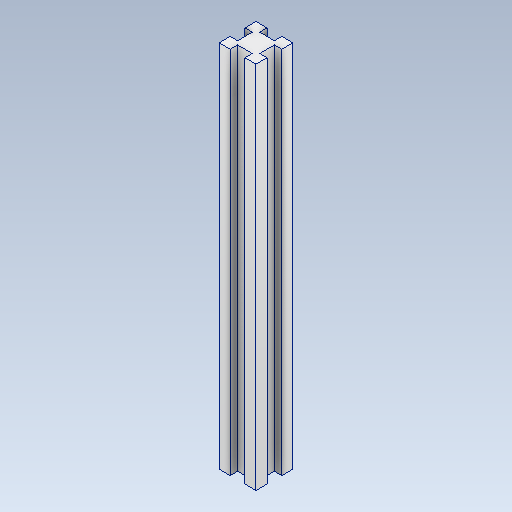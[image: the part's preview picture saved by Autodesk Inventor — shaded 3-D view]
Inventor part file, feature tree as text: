
AUTODESK INVENTOR PART (.ipt)
format: ipt  version: 2021 (Build 250183000, 183)  size: 115,712 bytes
history: native  units: mm
features: other x1, extrude x1, sketch x1
ambient origin geometry x8: Origin, YZ Plane, XZ Plane, XY Plane, X Axis, Y Axis, Z Axis, Center Point
bodies: Body1 (feature_tree)
feature tree (3):
  other  "Bryła1"
  extrude  "Wyciągnięcie proste1"  Depth=50.0mm
  sketch  "Szkic1"
